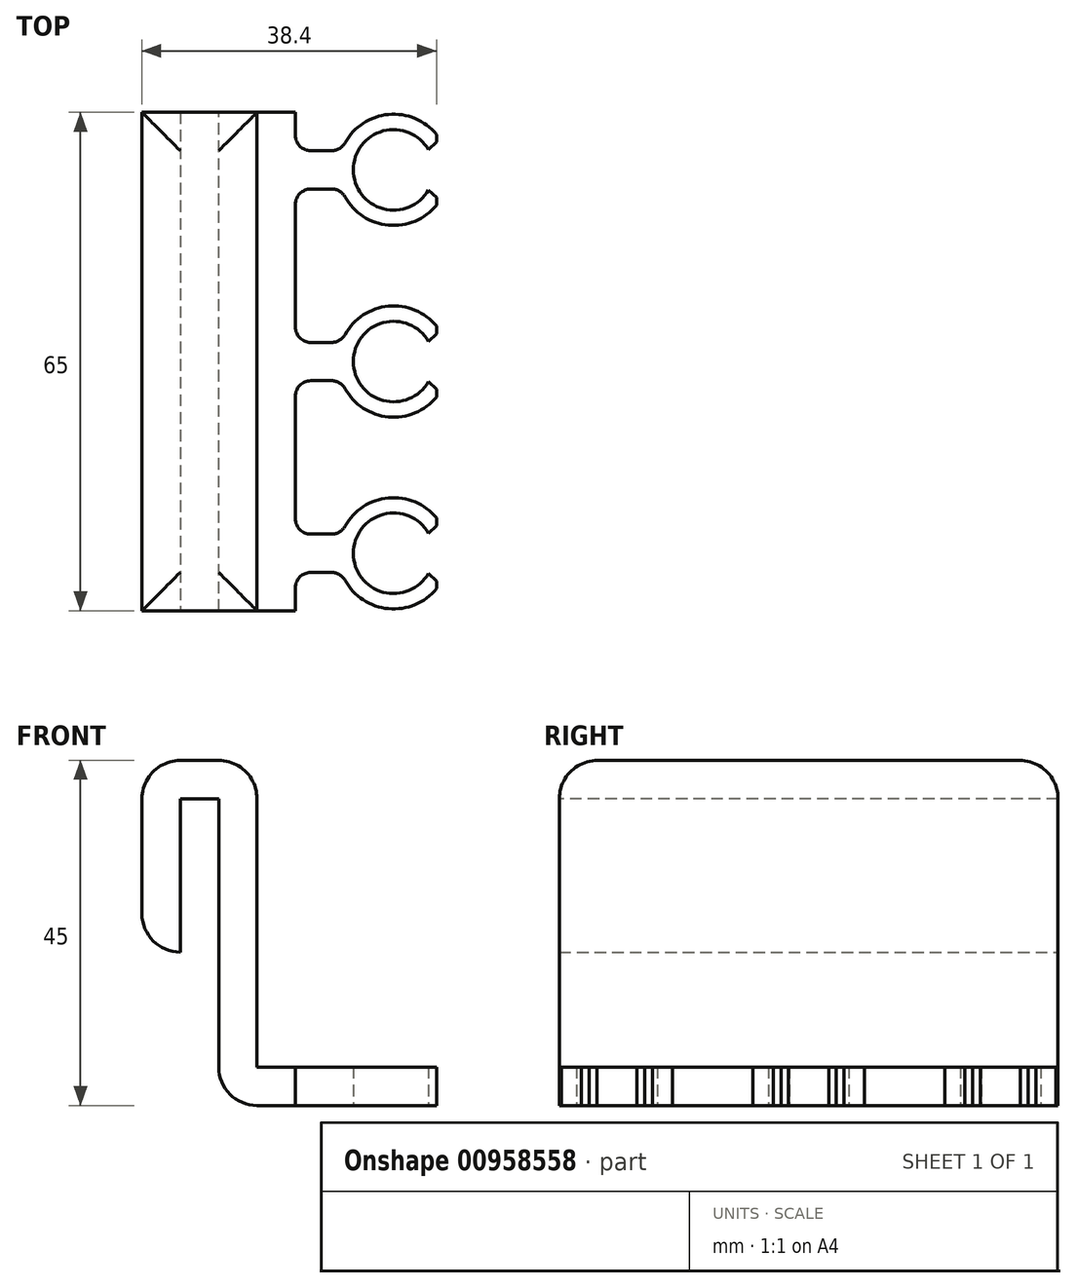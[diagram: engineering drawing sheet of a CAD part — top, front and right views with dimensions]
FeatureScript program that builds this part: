
annotation { "Feature Type Name" : "Feature", "Feature Type Description" : "" }
export const myFeature = defineFeature(function(context is Context, id is Id, definition is map)
    precondition{}
    {
        {
            var Q0;
            Q0=qCreatedBy(makeId("Top.planeOp"),FACE);
            var sketch = newSketch(context, id + "F0", { "sketchPlane" : qUnion([Q0])});
            skArc(sketch, "E0", {"start": v(4.55, 2.62) * mm, "mid": v(-5.25, 0) * mm, "end": v(4.55, -2.62) * mm});
            skLineSegment(sketch, "E1", {"start": v(4.55, -2.62) * mm, "end": v(5.59, -3.62) * mm});
            skLineSegment(sketch, "E2", {"start": v(5.59, -3.62) * mm, "end": v(5.59, -4.62) * mm});
            skLineSegment(sketch, "E3", {"start": v(4.55, 2.62) * mm, "end": v(5.59, 3.62) * mm});
            skLineSegment(sketch, "E4", {"start": v(5.59, 3.62) * mm, "end": v(5.59, 4.62) * mm});
            skArc(sketch, "E5", {"start": v(5.59, -4.62) * mm, "mid": v(-0.66, -7.22) * mm, "end": v(-6.33, -3.53) * mm});
            skArc(sketch, "E6", {"start": v(5.59, 4.62) * mm, "mid": v(-0.66, 7.22) * mm, "end": v(-6.33, 3.53) * mm});
            skLineSegment(sketch, "E7", {"start": v(-8.08, -2.5) * mm, "end": v(-10.8, -2.5) * mm});
            skLineSegment(sketch, "E8", {"start": v(-8.08, 2.5) * mm, "end": v(-10.8, 2.5) * mm});
            skLineSegment(sketch, "E9.0.1.1", {"start": v(-8.08, 22.5) * mm, "end": v(-10.8, 22.5) * mm});
            skLineSegment(sketch, "E9.0.1.2", {"start": v(-8.08, 27.5) * mm, "end": v(-10.8, 27.5) * mm});
            skArc(sketch, "E9.0.1.3", {"start": v(5.59, 29.62) * mm, "mid": v(-0.66, 32.22) * mm, "end": v(-6.33, 28.53) * mm});
            skArc(sketch, "E9.0.1.4", {"start": v(4.55, 27.62) * mm, "mid": v(-5.25, 25) * mm, "end": v(4.55, 22.38) * mm});
            skArc(sketch, "E9.0.1.5", {"start": v(5.59, 20.38) * mm, "mid": v(-0.66, 17.78) * mm, "end": v(-6.33, 21.47) * mm});
            skLineSegment(sketch, "E9.0.1.6", {"start": v(5.59, 21.38) * mm, "end": v(5.59, 20.38) * mm});
            skLineSegment(sketch, "E9.0.1.7", {"start": v(4.55, 22.38) * mm, "end": v(5.59, 21.38) * mm});
            skLineSegment(sketch, "E9.0.1.8", {"start": v(4.55, 27.62) * mm, "end": v(5.59, 28.62) * mm});
            skLineSegment(sketch, "E9.0.1.9", {"start": v(5.59, 28.62) * mm, "end": v(5.59, 29.62) * mm});
            skLineSegment(sketch, "E9.0.2.1", {"start": v(-8.08, 47.5) * mm, "end": v(-10.8, 47.5) * mm});
            skLineSegment(sketch, "E9.0.2.2", {"start": v(-8.08, 52.5) * mm, "end": v(-10.8, 52.5) * mm});
            skArc(sketch, "E9.0.2.3", {"start": v(5.59, 54.62) * mm, "mid": v(-0.66, 57.22) * mm, "end": v(-6.33, 53.53) * mm});
            skArc(sketch, "E9.0.2.4", {"start": v(4.55, 52.62) * mm, "mid": v(-5.25, 50) * mm, "end": v(4.55, 47.38) * mm});
            skArc(sketch, "E9.0.2.5", {"start": v(5.59, 45.38) * mm, "mid": v(-0.66, 42.78) * mm, "end": v(-6.33, 46.47) * mm});
            skLineSegment(sketch, "E9.0.2.6", {"start": v(5.59, 46.38) * mm, "end": v(5.59, 45.38) * mm});
            skLineSegment(sketch, "E9.0.2.7", {"start": v(4.55, 47.38) * mm, "end": v(5.59, 46.38) * mm});
            skLineSegment(sketch, "E9.0.2.8", {"start": v(4.55, 52.62) * mm, "end": v(5.59, 53.62) * mm});
            skLineSegment(sketch, "E9.0.2.9", {"start": v(5.59, 53.62) * mm, "end": v(5.59, 54.62) * mm});
            skLineSegment(sketch, "E10.bottom", {"start": v(-12.8, -7.5) * mm, "end": v(-22.8, -7.5) * mm});
            skLineSegment(sketch, "E10.top", {"start": v(-12.8, 57.5) * mm, "end": v(-22.8, 57.5) * mm});
            skLineSegment(sketch, "E10.left", {"start": v(-12.8, -7.5) * mm, "end": v(-12.8, -4.5) * mm});
            skLineSegment(sketch, "E10.right", {"start": v(-22.8, -7.5) * mm, "end": v(-22.8, 57.5) * mm});
            skArc(sketch, "E11.filletArc", {"start": v(-12.8, 4.5) * mm, "mid": v(-12.22, 3.09) * mm, "end": v(-10.8, 2.5) * mm});
            skArc(sketch, "E12.filletArc", {"start": v(-10.8, -2.5) * mm, "mid": v(-12.22, -3.09) * mm, "end": v(-12.8, -4.5) * mm});
            skPoint(sketch, "E13.visualSharp", {"position": v(-6.8, -2.5) * mm});
            skArc(sketch, "E13.filletArc", {"start": v(-6.33, -3.53) * mm, "mid": v(-7.07, -2.78) * mm, "end": v(-8.08, -2.5) * mm});
            skPoint(sketch, "E14.visualSharp", {"position": v(-6.8, 2.5) * mm});
            skArc(sketch, "E14.filletArc", {"start": v(-8.08, 2.5) * mm, "mid": v(-7.07, 2.78) * mm, "end": v(-6.33, 3.53) * mm});
            skLineSegment(sketch, "E15", {"start": v(-12.8, 4.5) * mm, "end": v(-12.8, 20.5) * mm});
            skArc(sketch, "E16.filletArc", {"start": v(-10.8, 22.5) * mm, "mid": v(-12.22, 21.91) * mm, "end": v(-12.8, 20.5) * mm});
            skPoint(sketch, "E17.visualSharp", {"position": v(-6.8, 22.5) * mm});
            skArc(sketch, "E17.filletArc", {"start": v(-6.33, 21.47) * mm, "mid": v(-7.07, 22.22) * mm, "end": v(-8.08, 22.5) * mm});
            skLineSegment(sketch, "E18", {"start": v(-12.8, 45.5) * mm, "end": v(-12.8, 29.5) * mm});
            skArc(sketch, "E19.filletArc", {"start": v(-12.8, 29.5) * mm, "mid": v(-12.22, 28.09) * mm, "end": v(-10.8, 27.5) * mm});
            skPoint(sketch, "E20.visualSharp", {"position": v(-6.8, 27.5) * mm});
            skArc(sketch, "E20.filletArc", {"start": v(-8.08, 27.5) * mm, "mid": v(-7.07, 27.78) * mm, "end": v(-6.33, 28.53) * mm});
            skArc(sketch, "E21.filletArc", {"start": v(-10.8, 47.5) * mm, "mid": v(-12.22, 46.91) * mm, "end": v(-12.8, 45.5) * mm});
            skPoint(sketch, "E22.visualSharp", {"position": v(-6.8, 47.5) * mm});
            skArc(sketch, "E22.filletArc", {"start": v(-6.33, 46.47) * mm, "mid": v(-7.07, 47.22) * mm, "end": v(-8.08, 47.5) * mm});
            skLineSegment(sketch, "E23", {"start": v(-12.8, 54.5) * mm, "end": v(-12.8, 57.5) * mm});
            skArc(sketch, "E24.filletArc", {"start": v(-12.8, 54.5) * mm, "mid": v(-12.22, 53.09) * mm, "end": v(-10.8, 52.5) * mm});
            skPoint(sketch, "E25.visualSharp", {"position": v(-6.8, 52.5) * mm});
            skArc(sketch, "E25.filletArc", {"start": v(-8.08, 52.5) * mm, "mid": v(-7.07, 52.78) * mm, "end": v(-6.33, 53.53) * mm});
            skSolve(sketch);
        }
        {
            var Q0;
            Q0 = qSketchRegion(id + "F0", true);
            extrude(context, id + "F1", {"entities" : qUnion([Q0]), "depth" : 5 * mm, "offsetDistance" : 25 * mm});
        }
        {
            var Q0;
            Q0=makeQuery(id+"F1.opExtrude","CAP_FACE",FACE,{"disambiguationData":[OSD([sQuery(id+"F0.wireOp",EDGE,"E0"),sQuery(id+"F0.wireOp",EDGE,"E1"),sQuery(id+"F0.wireOp",EDGE,"E2"),sQuery(id+"F0.wireOp",EDGE,"E3"),sQuery(id+"F0.wireOp",EDGE,"E4"),sQuery(id+"F0.wireOp",EDGE,"E5"),sQuery(id+"F0.wireOp",EDGE,"E6"),sQuery(id+"F0.wireOp",EDGE,"E7"),sQuery(id+"F0.wireOp",EDGE,"E8"),sQuery(id+"F0.wireOp",EDGE,"E9.0.1.1"),sQuery(id+"F0.wireOp",EDGE,"E9.0.1.2"),sQuery(id+"F0.wireOp",EDGE,"E9.0.1.3"),sQuery(id+"F0.wireOp",EDGE,"E9.0.1.4"),sQuery(id+"F0.wireOp",EDGE,"E9.0.1.5"),sQuery(id+"F0.wireOp",EDGE,"E9.0.1.6"),sQuery(id+"F0.wireOp",EDGE,"E9.0.1.7"),sQuery(id+"F0.wireOp",EDGE,"E9.0.1.8"),sQuery(id+"F0.wireOp",EDGE,"E9.0.1.9"),sQuery(id+"F0.wireOp",EDGE,"E9.0.2.1"),sQuery(id+"F0.wireOp",EDGE,"E9.0.2.2"),sQuery(id+"F0.wireOp",EDGE,"E9.0.2.3"),sQuery(id+"F0.wireOp",EDGE,"E9.0.2.4"),sQuery(id+"F0.wireOp",EDGE,"E9.0.2.5"),sQuery(id+"F0.wireOp",EDGE,"E9.0.2.6"),sQuery(id+"F0.wireOp",EDGE,"E9.0.2.7"),sQuery(id+"F0.wireOp",EDGE,"E9.0.2.8"),sQuery(id+"F0.wireOp",EDGE,"E9.0.2.9"),sQuery(id+"F0.wireOp",EDGE,"E10.bottom"),sQuery(id+"F0.wireOp",EDGE,"E10.top"),sQuery(id+"F0.wireOp",EDGE,"E10.left"),sQuery(id+"F0.wireOp",EDGE,"E10.right"),sQuery(id+"F0.wireOp",EDGE,"E11.filletArc"),sQuery(id+"F0.wireOp",EDGE,"E12.filletArc"),sQuery(id+"F0.wireOp",EDGE,"E13.filletArc"),sQuery(id+"F0.wireOp",EDGE,"E14.filletArc"),sQuery(id+"F0.wireOp",EDGE,"E15"),sQuery(id+"F0.wireOp",EDGE,"E16.filletArc"),sQuery(id+"F0.wireOp",EDGE,"E17.filletArc"),sQuery(id+"F0.wireOp",EDGE,"E18"),sQuery(id+"F0.wireOp",EDGE,"E19.filletArc"),sQuery(id+"F0.wireOp",EDGE,"E20.filletArc"),sQuery(id+"F0.wireOp",EDGE,"E21.filletArc"),sQuery(id+"F0.wireOp",EDGE,"E22.filletArc"),sQuery(id+"F0.wireOp",EDGE,"E23"),sQuery(id+"F0.wireOp",EDGE,"E24.filletArc"),sQuery(id+"F0.wireOp",EDGE,"E25.filletArc")])],"isStart":false});
            var sketch = newSketch(context, id + "F2", { "sketchPlane" : qUnion([Q0])});
            skLineSegment(sketch, "E26.bottom", {"start": v(-22.8, -7.5) * mm, "end": v(-17.8, -7.5) * mm});
            skLineSegment(sketch, "E26.top", {"start": v(-22.8, 57.5) * mm, "end": v(-17.8, 57.5) * mm});
            skLineSegment(sketch, "E26.left", {"start": v(-22.8, -7.5) * mm, "end": v(-22.8, 57.5) * mm});
            skLineSegment(sketch, "E26.right", {"start": v(-17.8, -7.5) * mm, "end": v(-17.8, 57.5) * mm});
            skSolve(sketch);
        }
        {
            var Q0;
            Q0=makeQuery(id+"F2.imprint","IMPRINT",FACE,{"disambiguationData":[TD([[makeQuery(id+"F2.imprint","IMPRINT",EDGE,{"derivedFrom":sQuery(id+"F2.wireOp",EDGE,"E26.bottom")}),-1.0]])]});
            extrude(context, id + "F3", {"entities" : qUnion([Q0]), "operationType" : NewBodyOperationType.ADD, "depth" : 40 * mm, "offsetDistance" : 25 * mm});
        }
        {
            var Q0;
            Q0=makeQuery(id+"F3.boolean.opBoolean","MERGE",FACE,{"derivedFrom":[makeQuery(id+"F1.opExtrude","SWEPT_FACE",FACE,{"disambiguationData":[OSD([sQuery(id+"F0.wireOp",EDGE,"E10.right")])]}),makeQuery(id+"F3.opExtrude","SWEPT_FACE",FACE,{"disambiguationData":[OSD([sQuery(id+"F2.wireOp",EDGE,"E26.left")])]})]});
            var sketch = newSketch(context, id + "F4", { "sketchPlane" : qUnion([Q0])});
            skLineSegment(sketch, "E27.bottom", {"start": v(-57.5, 40) * mm, "end": v(7.5, 40) * mm});
            skLineSegment(sketch, "E27.top", {"start": v(-57.5, 45) * mm, "end": v(7.5, 45) * mm});
            skLineSegment(sketch, "E27.left", {"start": v(-57.5, 40) * mm, "end": v(-57.5, 45) * mm});
            skLineSegment(sketch, "E27.right", {"start": v(7.5, 40) * mm, "end": v(7.5, 45) * mm});
            skSolve(sketch);
        }
        {
            var Q0;
            Q0=makeQuery(id+"F4.imprint","IMPRINT",FACE,{"disambiguationData":[TD([[makeQuery(id+"F4.imprint","IMPRINT",EDGE,{"derivedFrom":sQuery(id+"F4.wireOp",EDGE,"E27.bottom")}),1.0]])]});
            extrude(context, id + "F5", {"entities" : qUnion([Q0]), "operationType" : NewBodyOperationType.ADD, "depth" : 5 * mm, "offsetDistance" : 25 * mm});
        }
        {
            var Q0;
            Q0=makeQuery(id+"F5.opExtrude","SWEPT_FACE",FACE,{"disambiguationData":[OSD([sQuery(id+"F4.wireOp",EDGE,"E27.top")])]});
            var sketch = newSketch(context, id + "F6", { "sketchPlane" : qUnion([Q0])});
            skLineSegment(sketch, "E28.bottom", {"start": v(-27.8, 57.5) * mm, "end": v(-32.8, 57.5) * mm});
            skLineSegment(sketch, "E28.top", {"start": v(-27.8, -7.5) * mm, "end": v(-32.8, -7.5) * mm});
            skLineSegment(sketch, "E28.left", {"start": v(-27.8, 57.5) * mm, "end": v(-27.8, -7.5) * mm});
            skLineSegment(sketch, "E28.right", {"start": v(-32.8, 57.5) * mm, "end": v(-32.8, -7.5) * mm});
            skSolve(sketch);
        }
        {
            var Q0;
            Q0=makeQuery(id+"F6.imprint","IMPRINT",FACE,{"disambiguationData":[TD([[makeQuery(id+"F6.imprint","IMPRINT",EDGE,{"derivedFrom":sQuery(id+"F6.wireOp",EDGE,"E28.bottom")}),1.0]])]});
            extrude(context, id + "F7", {"entities" : qUnion([Q0]), "operationType" : NewBodyOperationType.ADD, "oppositeDirection" : true, "depth" : 25 * mm, "offsetDistance" : 25 * mm});
        }
        {
            var Q0;
            Q0=makeQuery(id+"F7.opExtrude","CAP_EDGE",EDGE,{"disambiguationData":[OSD([sQuery(id+"F6.wireOp",EDGE,"E28.right")])],"isStart":true});
            var Q1;
            Q1=makeQuery(id+"F5.opExtrude","SWEPT_EDGE",EDGE,{"disambiguationData":[OSD([sQuery(id+"F4.wireOp",EDGE,"E27.top"),sQuery(id+"F4.wireOp",EDGE,"E27.right")])]});
            var Q2;
            Q2=makeQuery(id+"F7.opExtrude","CAP_EDGE",EDGE,{"disambiguationData":[OSD([sQuery(id+"F6.wireOp",EDGE,"E28.top")])],"isStart":true});
            var Q3;
            Q3=makeQuery(id+"F3.opExtrude","CAP_EDGE",EDGE,{"disambiguationData":[OSD([sQuery(id+"F2.wireOp",EDGE,"E26.bottom")])],"isStart":false});
            var Q4;
            Q4=makeQuery(id+"F3.opExtrude","CAP_EDGE",EDGE,{"disambiguationData":[OSD([sQuery(id+"F2.wireOp",EDGE,"E26.right")])],"isStart":false});
            var Q5;
            Q5=makeQuery(id+"F3.opExtrude","CAP_EDGE",EDGE,{"disambiguationData":[OSD([sQuery(id+"F2.wireOp",EDGE,"E26.top")])],"isStart":false});
            var Q6;
            Q6=makeQuery(id+"F5.opExtrude","SWEPT_EDGE",EDGE,{"disambiguationData":[OSD([sQuery(id+"F4.wireOp",EDGE,"E27.top"),sQuery(id+"F4.wireOp",EDGE,"E27.left")])]});
            var Q7;
            Q7=makeQuery(id+"F7.opExtrude","CAP_EDGE",EDGE,{"disambiguationData":[OSD([sQuery(id+"F6.wireOp",EDGE,"E28.bottom")])],"isStart":true});
            var Q8;
            Q8=makeQuery(id+"F3.opExtrude","CAP_EDGE",EDGE,{"disambiguationData":[OSD([sQuery(id+"F2.wireOp",EDGE,"E26.right")])],"isStart":true});
            var Q9;
            Q9=makeQuery(id+"F1.opExtrude","CAP_EDGE",EDGE,{"disambiguationData":[OSD([sQuery(id+"F0.wireOp",EDGE,"E10.right")])],"isStart":true});
            var Q10;
            Q10=makeQuery(id+"F7.opExtrude","CAP_EDGE",EDGE,{"disambiguationData":[OSD([sQuery(id+"F6.wireOp",EDGE,"E28.right")])],"isStart":false});
            fillet(context, id + "F8", {"entities" : qUnion([Q0, Q1, Q2, Q3, Q4, Q5, Q6, Q7, Q8, Q9, Q10]), "radius" : 5 * mm, "tangentPropagation" : true, "allowEdgeOverflow" : false});
        }
    });
